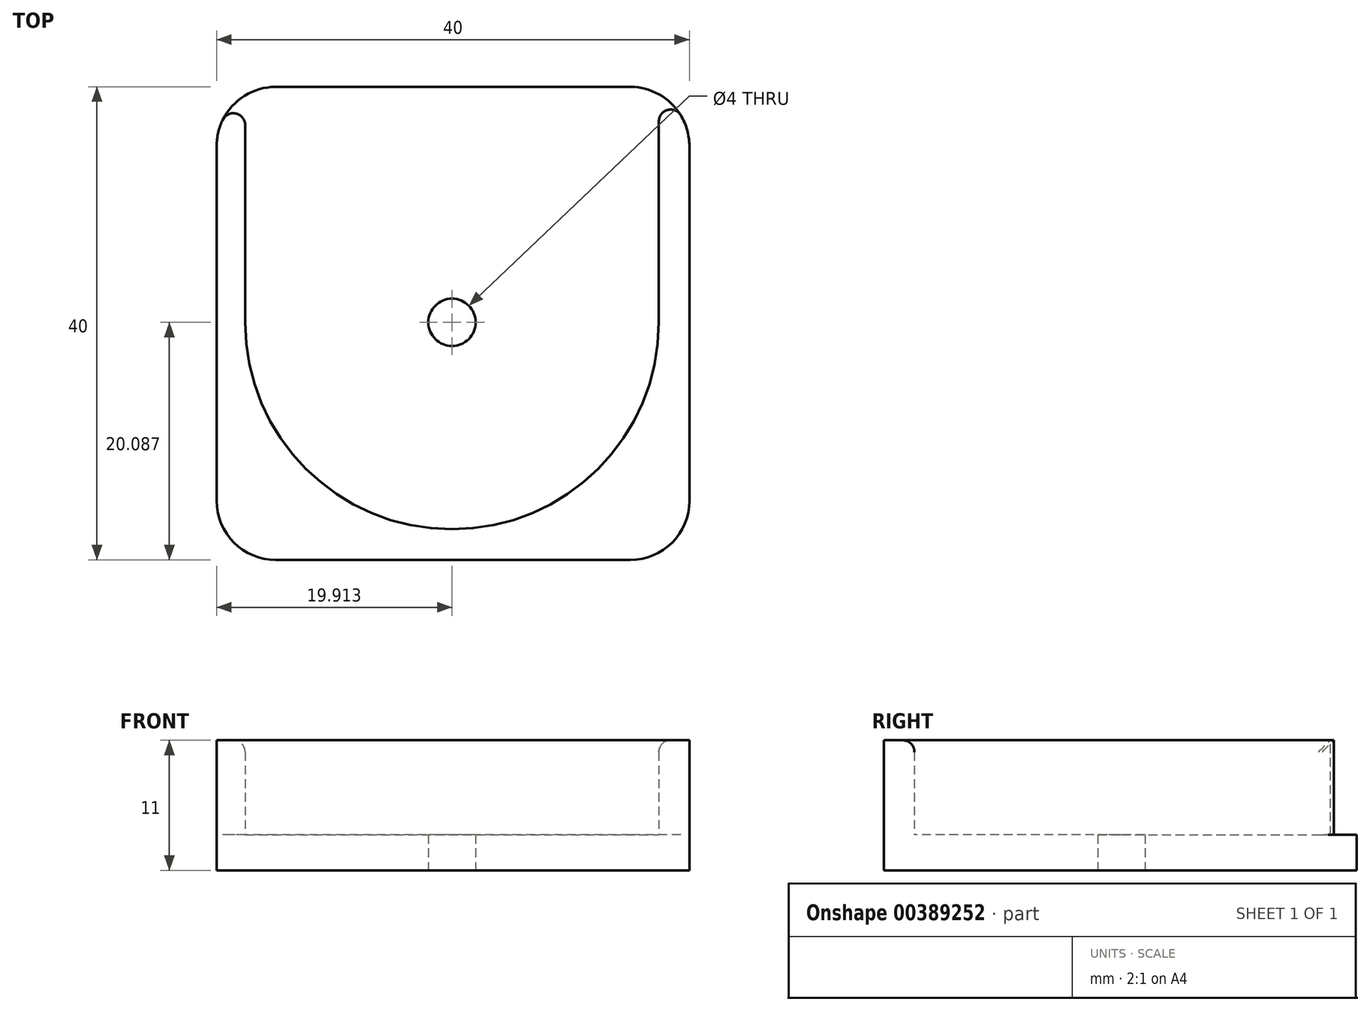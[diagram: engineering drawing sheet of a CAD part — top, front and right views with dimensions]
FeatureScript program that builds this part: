
annotation { "Feature Type Name" : "Feature", "Feature Type Description" : "" }
export const myFeature = defineFeature(function(context is Context, id is Id, definition is map)
    precondition{}
    {
        {
            var Q0;
            Q0=qCreatedBy(makeId("Top.planeOp"),FACE);
            var sketch = newSketch(context, id + "F0", { "sketchPlane" : qUnion([Q0])});
            skLineSegment(sketch, "E0.bottom", {"start": v(0, 0) * mm, "end": v(-40, 0) * mm});
            skLineSegment(sketch, "E0.top", {"start": v(0, 40) * mm, "end": v(-40, 40) * mm});
            skLineSegment(sketch, "E0.left", {"start": v(0, 0) * mm, "end": v(0, 40) * mm});
            skLineSegment(sketch, "E0.right", {"start": v(-40, 0) * mm, "end": v(-40, 40) * mm});
            skCircle(sketch, "E1", {"center": v(-20.09, 20.09) * mm, "radius": 17.5 * mm});
            skLineSegment(sketch, "E2", {"start": v(-37.59, 20.09) * mm, "end": v(-37.59, 40) * mm});
            skLineSegment(sketch, "E3", {"start": v(-2.59, 20.09) * mm, "end": v(-2.59, 40) * mm});
            skCircle(sketch, "E4", {"center": v(-20.09, 20.09) * mm, "radius": 2 * mm});
            skSolve(sketch);
        }
        {
            var Q0;
            Q0=makeQuery(id+"F0.imprint","IMPRINT",FACE,{"disambiguationData":[TD([[makeQuery(id+"F0.imprint","IMPRINT",EDGE,{"derivedFrom":sQuery(id+"F0.wireOp",EDGE,"E0.bottom")}),-1.0]])]});
            extrude(context, id + "F1", {"entities" : qUnion([Q0]), "depth" : 11 * mm});
        }
        {
            var Q0;
            {var subQ0=sQuery(id+"F0.wireOp",EDGE,"E2");Q0=makeQuery(id+"F0.imprint","IMPRINT",FACE,{"disambiguationData":[TD([[makeQuery(id+"F0.imprint","IMPRINT",EDGE,{"derivedFrom":subQ0}),-1.0]])]});}
            var Q1;
            {var subQ0=sQuery(id+"F0.wireOp",EDGE,"E1");var subQ1=makeQuery(id+"F0.imprint","INTERSECT",VERTEX,{"derivedFrom":[subQ0,sQuery(id+"F0.wireOp",EDGE,"E2")]});Q1=makeQuery(id+"F0.imprint","IMPRINT",FACE,{"disambiguationData":[TD([[makeQuery(id+"F0.imprint","IMPRINT",EDGE,{"disambiguationData":[TD([[subQ1,1.0]])],"derivedFrom":subQ0}),1.0]])]});}
            extrude(context, id + "F2", {"entities" : qUnion([Q0, Q1]), "operationType" : NewBodyOperationType.ADD, "depth" : 3 * mm});
        }
        {
            var Q0;
            Q0=makeQuery(id+"F1.opExtrude","SWEPT_EDGE",EDGE,{"disambiguationData":[OSD([sQuery(id+"F0.wireOp",EDGE,"E0.bottom"),sQuery(id+"F0.wireOp",EDGE,"E0.right")])]});
            var Q1;
            Q1=makeQuery(id+"F1.opExtrude","SWEPT_EDGE",EDGE,{"disambiguationData":[OSD([sQuery(id+"F0.wireOp",EDGE,"E0.bottom"),sQuery(id+"F0.wireOp",EDGE,"E0.left")])]});
            var Q2;
            Q2=makeQuery(id+"F1.opExtrude","SWEPT_EDGE",EDGE,{"disambiguationData":[OSD([sQuery(id+"F0.wireOp",EDGE,"E0.top"),sQuery(id+"F0.wireOp",EDGE,"E0.left")])]});
            var Q3;
            Q3=makeQuery(id+"F1.opExtrude","SWEPT_EDGE",EDGE,{"disambiguationData":[OSD([sQuery(id+"F0.wireOp",EDGE,"E0.top"),sQuery(id+"F0.wireOp",EDGE,"E0.right")])]});
            fillet(context, id + "F3", {"entities" : qUnion([Q0, Q1, Q2, Q3]), "radius" : 5 * mm, "tangentPropagation" : true, "allowEdgeOverflow" : false});
        }
        {
            var Q0;
            Q0=makeQuery(id+"F1.opExtrude","CAP_EDGE",EDGE,{"disambiguationData":[OSD([sQuery(id+"F0.wireOp",EDGE,"E1")])],"isStart":false});
            var Q1;
            Q1=makeQuery(id+"F1.opExtrude","CAP_EDGE",EDGE,{"disambiguationData":[OSD([sQuery(id+"F0.wireOp",EDGE,"E2")])],"isStart":false});
            var Q2;
            Q2=makeQuery(id+"F3.opFillet","BLEND_EDGE",EDGE,{"blendedFrom":[makeQuery(id+"F1.opExtrude","SWEPT_EDGE",EDGE,{"disambiguationData":[OSD([sQuery(id+"F0.wireOp",EDGE,"E0.top"),sQuery(id+"F0.wireOp",EDGE,"E0.left")])]}),makeQuery(id+"F1.opExtrude","SWEPT_FACE",FACE,{"disambiguationData":[OSD([sQuery(id+"F0.wireOp",EDGE,"E3")])]})],"blendedInto":[makeQuery(id+"F1.opExtrude","SWEPT_FACE",FACE,{"disambiguationData":[OSD([sQuery(id+"F0.wireOp",EDGE,"E3")])]})]});
            var Q3;
            Q3=makeQuery(id+"F3.opFillet","BLEND_EDGE",EDGE,{"blendedFrom":[makeQuery(id+"F1.opExtrude","SWEPT_EDGE",EDGE,{"disambiguationData":[OSD([sQuery(id+"F0.wireOp",EDGE,"E0.top"),sQuery(id+"F0.wireOp",EDGE,"E0.right")])]}),makeQuery(id+"F1.opExtrude","SWEPT_FACE",FACE,{"disambiguationData":[OSD([sQuery(id+"F0.wireOp",EDGE,"E2")])]})],"blendedInto":[makeQuery(id+"F1.opExtrude","SWEPT_FACE",FACE,{"disambiguationData":[OSD([sQuery(id+"F0.wireOp",EDGE,"E2")])]})]});
            fillet(context, id + "F4", {"entities" : qUnion([Q0, Q1, Q2, Q3]), "radius" : 1 * mm, "tangentPropagation" : true, "allowEdgeOverflow" : false});
        }
    });
